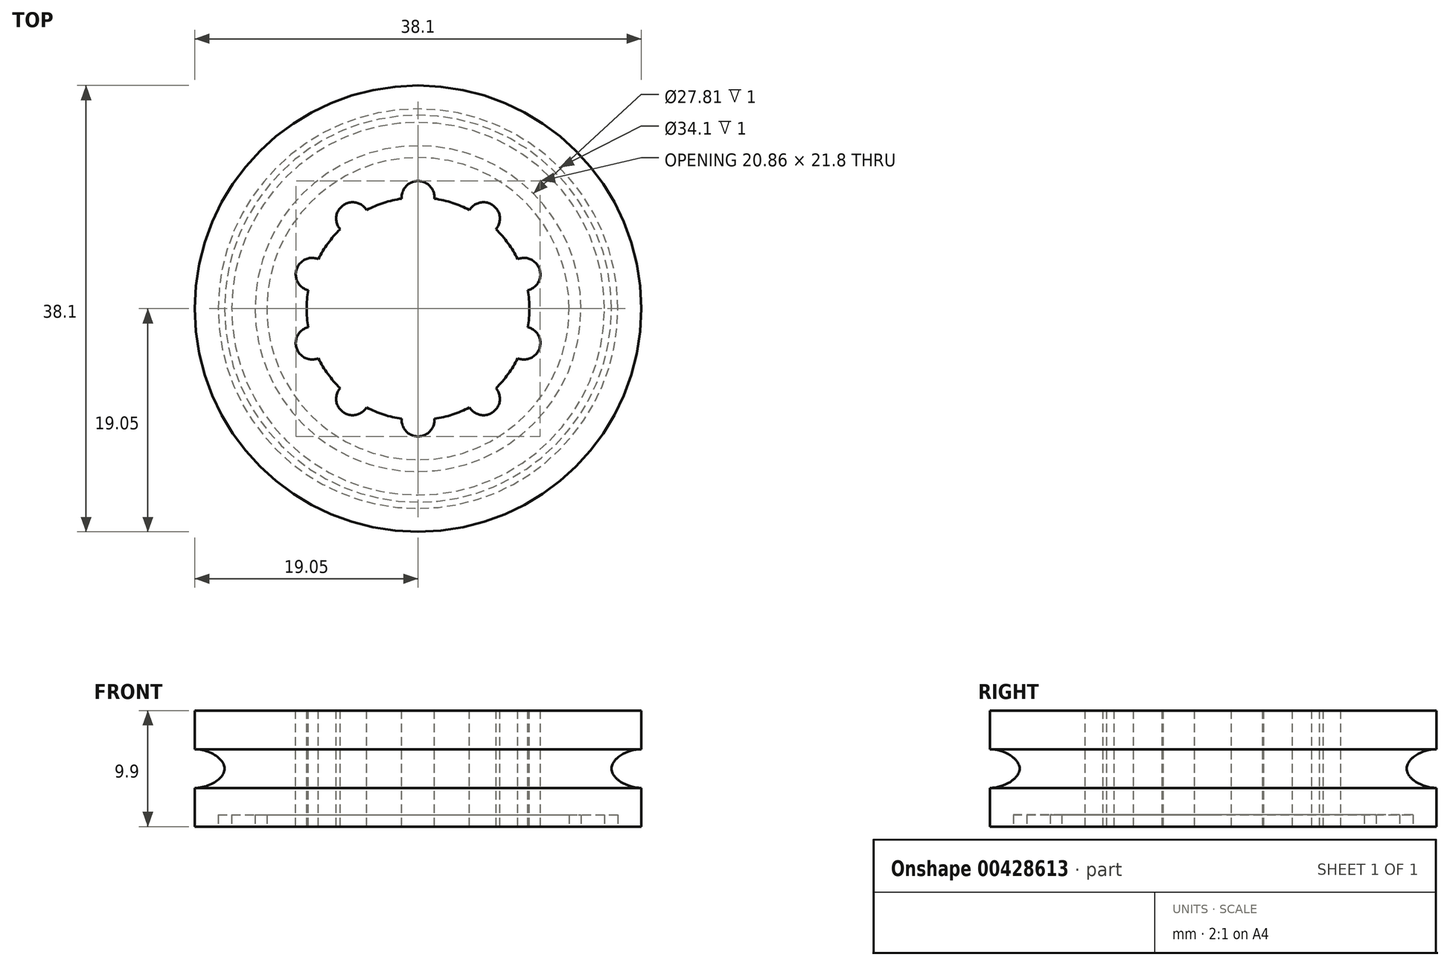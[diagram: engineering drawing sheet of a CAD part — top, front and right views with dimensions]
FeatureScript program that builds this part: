
annotation { "Feature Type Name" : "Feature", "Feature Type Description" : "" }
export const myFeature = defineFeature(function(context is Context, id is Id, definition is map)
    precondition{}
    {
        {
            var Q0;
            Q0=qCreatedBy(makeId("Front.planeOp"),FACE);
            var sketch = newSketch(context, id + "F0", { "sketchPlane" : qUnion([Q0])});
            skLineSegment(sketch, "E0", {"start": v(0, 4.95) * mm, "end": v(-19.05, 4.95) * mm});
            skLineSegment(sketch, "E1", {"start": v(-19.05, 4.95) * mm, "end": v(-19.05, 1.65) * mm});
            skLineSegment(sketch, "E2", {"start": v(-19.05, 1.65) * mm, "end": v(-16.51, 1.65) * mm});
            skLineSegment(sketch, "E3", {"start": v(-16.51, 1.65) * mm, "end": v(-16.51, 0) * mm});
            skLineSegment(sketch, "E4", {"start": v(0, 4.95) * mm, "end": v(0, 0) * mm});
            skLineSegment(sketch, "E5", {"start": v(0, 0) * mm, "end": v(-16.51, 0) * mm});
            skLineSegment(sketch, "E6", {"start": v(0, 0) * mm, "end": v(0, 23.56) * mm, "construction": true});
            skFitSpline(sketch, "E7", {"points": [v(-19.05, 1.65) * mm, v(-16.51, 0) * mm], "startDerivative": vector(3.81, 0) * mm, "endDerivative": vector(0, -2.48) * mm});
            skSolve(sketch);
        }
        {
            var Q0;
            Q0=qSketchRegion(id+"F0",true);
            var Q1;
            Q1=sQuery(id+"F0.wireOp",EDGE,"E6");
            revolve(context, id + "F1", {"entities" : qUnion([Q0]), "axis" : qUnion([Q1]), "revolveType" : RevolveType.FULL});
        }
        {
            var Q0;
            Q0=makeQuery(id+"F1.opRevolve","SWEPT_BODY",BODY,{"disambiguationData":[OSD([sQuery(id+"F0.wireOp",EDGE,"E0"),sQuery(id+"F0.wireOp",EDGE,"E1"),sQuery(id+"F0.wireOp",EDGE,"E2"),sQuery(id+"F0.wireOp",EDGE,"E3"),sQuery(id+"F0.wireOp",EDGE,"E4"),sQuery(id+"F0.wireOp",EDGE,"E5")])]});
            var Q1;
            Q1=qCreatedBy(makeId("Top.planeOp"),FACE);
            mirror(context, id + "F2", {"operationType" : NewBodyOperationType.ADD, "entities" : qUnion([Q0]), "mirrorPlane" : qUnion([Q1])});
        }
        {
            var Q0;
            Q0=makeQuery(id+"F1.opRevolve","SWEPT_FACE",FACE,{"disambiguationData":[OSD([sQuery(id+"F0.wireOp",EDGE,"E0")])]});
            var sketch = newSketch(context, id + "F3", { "sketchPlane" : qUnion([Q0])});
            skCircle(sketch, "E8", {"center": v(0, 0) * mm, "radius": 9.5 * mm});
            skCircle(sketch, "E9", {"center": v(0, 9.5) * mm, "radius": 1.4 * mm});
            skCircle(sketch, "E10.1.0", {"center": v(-5.58, 7.69) * mm, "radius": 1.4 * mm});
            skCircle(sketch, "E10.2.0", {"center": v(-9.04, 2.94) * mm, "radius": 1.4 * mm});
            skCircle(sketch, "E10.3.0", {"center": v(-9.04, -2.94) * mm, "radius": 1.4 * mm});
            skCircle(sketch, "E10.4.0", {"center": v(-5.58, -7.69) * mm, "radius": 1.4 * mm});
            skCircle(sketch, "E10.5.0", {"center": v(0, -9.5) * mm, "radius": 1.4 * mm});
            skCircle(sketch, "E10.6.0", {"center": v(5.58, -7.69) * mm, "radius": 1.4 * mm});
            skCircle(sketch, "E10.7.0", {"center": v(9.04, -2.94) * mm, "radius": 1.4 * mm});
            skCircle(sketch, "E10.8.0", {"center": v(9.04, 2.94) * mm, "radius": 1.4 * mm});
            skCircle(sketch, "E10.9.0", {"center": v(5.58, 7.69) * mm, "radius": 1.4 * mm});
            skSolve(sketch);
        }
        {
            var Q0;
            Q0=qSketchRegion(id+"F3",true);
            extrude(context, id + "F4", {"entities" : qUnion([Q0]), "operationType" : NewBodyOperationType.REMOVE, "endBound" : BoundingType.THROUGH_ALL, "oppositeDirection" : true, "depth" : 25.4 * mm});
        }
        {
            var Q0;
            Q0=makeQuery(id+"F2.opPattern","COPY",FACE,{"derivedFrom":makeQuery(id+"F1.opRevolve","SWEPT_FACE",FACE,{"disambiguationData":[OSD([sQuery(id+"F0.wireOp",EDGE,"E0")])]}),"instanceName":"1"});
            var sketch = newSketch(context, id + "F5", { "sketchPlane" : qUnion([Q0])});
            skCircle(sketch, "E11", {"center": v(0, 0) * mm, "radius": 9.5 * mm, "construction": true});
            skCircle(sketch, "E12", {"center": v(0, 0) * mm, "radius": 17.05 * mm});
            skLineSegment(sketch, "E13", {"start": v(0, 19.05) * mm, "end": v(0, 9.5) * mm, "construction": true});
            skCircle(sketch, "E14", {"center": v(0, 0) * mm, "radius": 14.9 * mm, "construction": true});
            skCircle(sketch, "E15", {"center": v(0, 0) * mm, "radius": 13.9 * mm});
            skCircle(sketch, "E16", {"center": v(0, 0) * mm, "radius": 15.9 * mm});
            skCircle(sketch, "E17", {"center": v(0, 0) * mm, "radius": 10.9 * mm, "construction": true});
            skCircle(sketch, "E18", {"center": v(0, 0) * mm, "radius": 12.9 * mm});
            skLineSegment(sketch, "E19", {"start": v(0, -12.9) * mm, "end": v(0, -17.05) * mm, "construction": true});
            skSolve(sketch);
        }
        {
            var Q0;
            Q0=makeQuery(id+"F5.imprint","IMPRINT",FACE,{"disambiguationData":[TD([[makeQuery(id+"F5.imprint","IMPRINT",EDGE,{"derivedFrom":sQuery(id+"F5.wireOp",EDGE,"E15")}),1.0]])]});
            var Q1;
            Q1=makeQuery(id+"F5.imprint","IMPRINT",FACE,{"disambiguationData":[TD([[makeQuery(id+"F5.imprint","IMPRINT",EDGE,{"derivedFrom":sQuery(id+"F5.wireOp",EDGE,"E12")}),1.0]])]});
            extrude(context, id + "F6", {"entities" : qUnion([Q0, Q1]), "operationType" : NewBodyOperationType.REMOVE, "oppositeDirection" : true, "depth" : 1 * mm});
        }
    });
